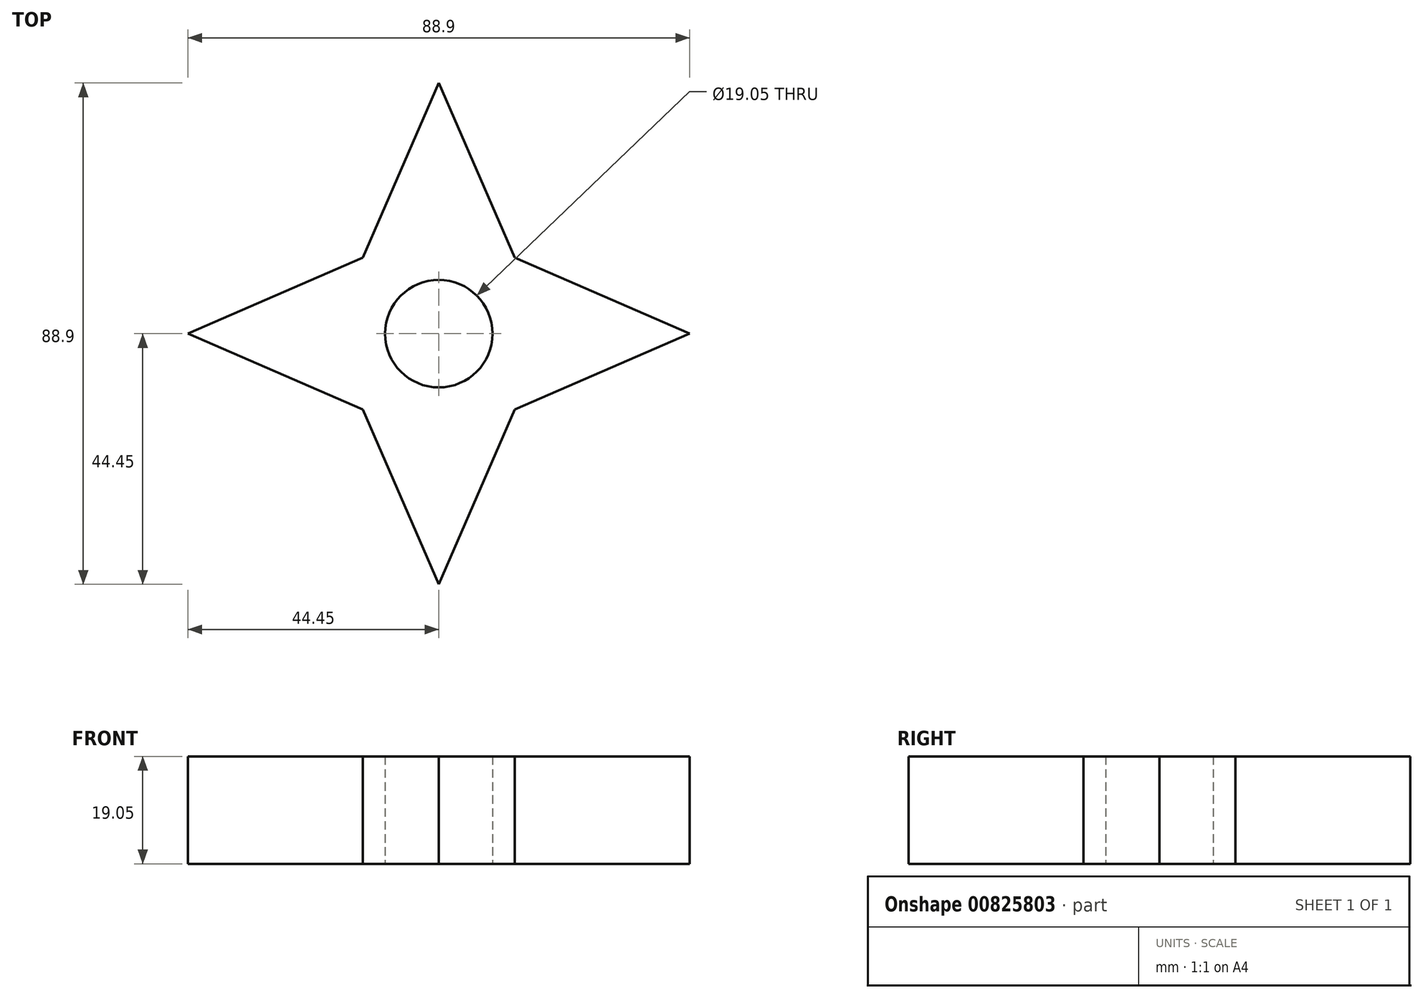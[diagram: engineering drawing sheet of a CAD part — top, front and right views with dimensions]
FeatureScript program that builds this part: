
annotation { "Feature Type Name" : "Feature", "Feature Type Description" : "" }
export const myFeature = defineFeature(function(context is Context, id is Id, definition is map)
    precondition{}
    {
        {
            var Q0;
            Q0=qCreatedBy(makeId("Top.planeOp"),FACE);
            var sketch = newSketch(context, id + "F0", { "sketchPlane" : qUnion([Q0])});
            skCircle(sketch, "E0", {"center": v(0, 0) * mm, "radius": 9.53 * mm});
            skLineSegment(sketch, "E1", {"start": v(0, 44.45) * mm, "end": v(13.47, 13.47) * mm});
            skLineSegment(sketch, "E2", {"start": v(44.45, 0) * mm, "end": v(13.47, 13.47) * mm});
            skLineSegment(sketch, "E3", {"start": v(0, -44.45) * mm, "end": v(13.47, -13.47) * mm});
            skLineSegment(sketch, "E4", {"start": v(13.47, -13.47) * mm, "end": v(44.45, 0) * mm});
            skLineSegment(sketch, "E5", {"start": v(-44.45, 0) * mm, "end": v(-13.47, -13.47) * mm});
            skLineSegment(sketch, "E6", {"start": v(-13.47, -13.47) * mm, "end": v(0, -44.45) * mm});
            skLineSegment(sketch, "E7", {"start": v(0, 44.45) * mm, "end": v(-13.47, 13.47) * mm});
            skLineSegment(sketch, "E8", {"start": v(-13.47, 13.47) * mm, "end": v(-44.45, 0) * mm});
            skSolve(sketch);
        }
        {
            var Q0;
            Q0=makeQuery(id+"F0.imprint","IMPRINT",FACE,{"disambiguationData":[TD([[makeQuery(id+"F0.imprint","IMPRINT",EDGE,{"derivedFrom":sQuery(id+"F0.wireOp",EDGE,"E0")}),-1.0]])]});
            extrude(context, id + "F1", {"entities" : qUnion([Q0]), "depth" : 19.05 * mm, "offsetDistance" : 25.4 * mm});
        }
    });
